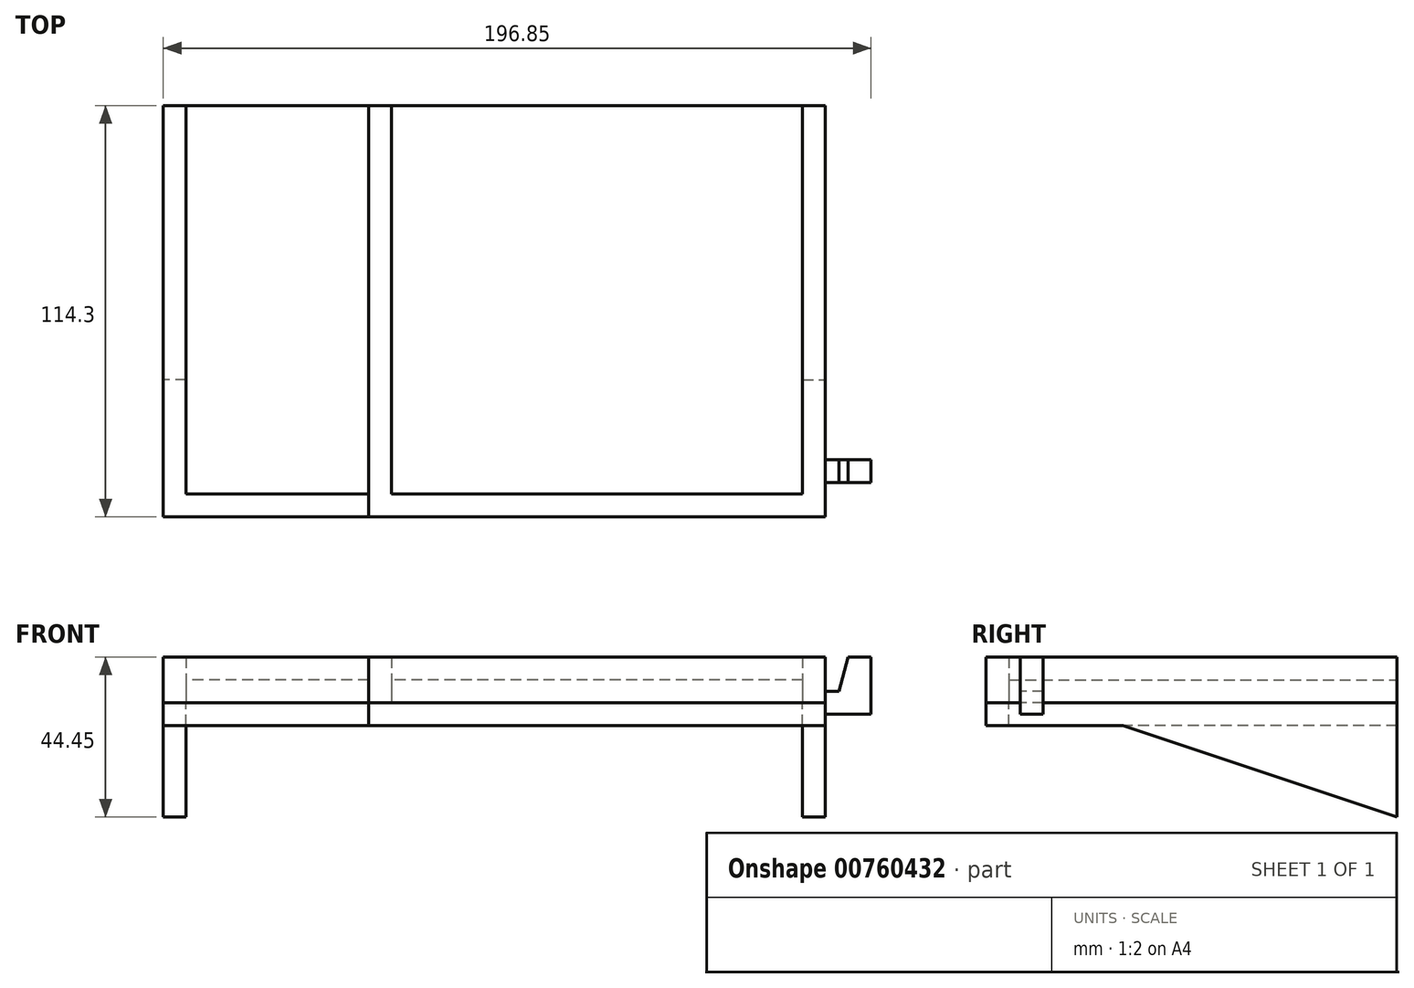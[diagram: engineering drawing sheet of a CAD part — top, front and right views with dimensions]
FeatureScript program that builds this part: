
annotation { "Feature Type Name" : "Feature", "Feature Type Description" : "" }
export const myFeature = defineFeature(function(context is Context, id is Id, definition is map)
    precondition{}
    {
        {
            var Q0;
            Q0=qCreatedBy(makeId("Top.planeOp"),FACE);
            var sketch = newSketch(context, id + "F0", { "sketchPlane" : qUnion([Q0])});
            skLineSegment(sketch, "E0.bottom", {"start": v(63.5, 57.15) * mm, "end": v(-63.5, 57.15) * mm});
            skLineSegment(sketch, "E0.top", {"start": v(63.5, -57.15) * mm, "end": v(-63.5, -57.15) * mm});
            skLineSegment(sketch, "E0.left", {"start": v(63.5, 57.15) * mm, "end": v(63.5, -57.15) * mm});
            skLineSegment(sketch, "E0.right", {"start": v(-63.5, 57.15) * mm, "end": v(-63.5, -57.15) * mm});
            skPoint(sketch, "E0.middle", {"position": v(0, 0) * mm});
            skLineSegment(sketch, "E1.bottom", {"start": v(-63.5, 57.15) * mm, "end": v(-57.15, 57.15) * mm});
            skLineSegment(sketch, "E1.top", {"start": v(-63.5, -57.15) * mm, "end": v(-57.15, -57.15) * mm});
            skLineSegment(sketch, "E1.right", {"start": v(-57.15, 57.15) * mm, "end": v(-57.15, -57.15) * mm});
            skLineSegment(sketch, "E2.bottom", {"start": v(-63.5, 57.15) * mm, "end": v(63.5, 57.15) * mm});
            skLineSegment(sketch, "E2.top", {"start": v(-63.5, 50.8) * mm, "end": v(63.5, 50.8) * mm});
            skLineSegment(sketch, "E2.left", {"start": v(-63.5, 57.15) * mm, "end": v(-63.5, 50.8) * mm});
            skLineSegment(sketch, "E2.right", {"start": v(63.5, 57.15) * mm, "end": v(63.5, 50.8) * mm});
            skLineSegment(sketch, "E3.bottom", {"start": v(-63.5, -57.15) * mm, "end": v(63.5, -57.15) * mm});
            skLineSegment(sketch, "E3.top", {"start": v(-63.5, -50.8) * mm, "end": v(63.5, -50.8) * mm});
            skLineSegment(sketch, "E3.left", {"start": v(-63.5, -57.15) * mm, "end": v(-63.5, -50.8) * mm});
            skLineSegment(sketch, "E3.right", {"start": v(63.5, -57.15) * mm, "end": v(63.5, -50.8) * mm});
            skLineSegment(sketch, "E4.bottom", {"start": v(63.5, -57.15) * mm, "end": v(57.15, -57.15) * mm});
            skLineSegment(sketch, "E4.top", {"start": v(63.5, 57.15) * mm, "end": v(57.15, 57.15) * mm});
            skLineSegment(sketch, "E4.left", {"start": v(63.5, -57.15) * mm, "end": v(63.5, 57.15) * mm});
            skLineSegment(sketch, "E4.right", {"start": v(57.15, -57.15) * mm, "end": v(57.15, 57.15) * mm});
            skLineSegment(sketch, "E5.bottom", {"start": v(-63.5, 57.15) * mm, "end": v(-114.3, 57.15) * mm});
            skLineSegment(sketch, "E5.left", {"start": v(-63.5, 57.15) * mm, "end": v(-63.5, -57.37) * mm});
            skLineSegment(sketch, "E5.right", {"start": v(-114.3, 57.15) * mm, "end": v(-114.3, -57.37) * mm});
            skLineSegment(sketch, "E6.bottom", {"start": v(-114.3, 57.15) * mm, "end": v(-120.65, 57.15) * mm});
            skLineSegment(sketch, "E6.top", {"start": v(-114.3, -57.15) * mm, "end": v(-120.65, -57.15) * mm});
            skLineSegment(sketch, "E6.left", {"start": v(-114.3, 57.15) * mm, "end": v(-114.3, -57.15) * mm});
            skLineSegment(sketch, "E6.right", {"start": v(-120.65, 57.15) * mm, "end": v(-120.65, -57.15) * mm});
            skLineSegment(sketch, "E7", {"start": v(-63.5, 50.8) * mm, "end": v(-114.3, 50.8) * mm});
            skLineSegment(sketch, "E8", {"start": v(-63.5, -50.8) * mm, "end": v(-63.5, 50.8) * mm});
            skLineSegment(sketch, "E9", {"start": v(-57.15, -57.15) * mm, "end": v(-57.15, 57.15) * mm});
            skLineSegment(sketch, "E10", {"start": v(-63.5, -50.8) * mm, "end": v(-114.3, -50.8) * mm});
            skLineSegment(sketch, "E11", {"start": v(-114.3, -50.8) * mm, "end": v(-114.3, -57.15) * mm});
            skLineSegment(sketch, "E12", {"start": v(-63.5, -57.15) * mm, "end": v(-114.3, -57.15) * mm});
            skSolve(sketch);
        }
        {
            var Q0;
            {var subQ0=sQuery(id+"F0.wireOp",EDGE,"E7");Q0=makeQuery(id+"F0.imprint","IMPRINT",FACE,{"disambiguationData":[TD([[makeQuery(id+"F0.imprint","IMPRINT",EDGE,{"derivedFrom":subQ0}),1.0]])]});}
            var Q1;
            {var subQ0=sQuery(id+"F0.wireOp",EDGE,"E2.top");var subQ1=sQuery(id+"F0.wireOp",EDGE,"E1.right");var subQ2=makeQuery(id+"F0.imprint","INTERSECT",VERTEX,{"derivedFrom":[subQ1,subQ0]});Q1=makeQuery(id+"F0.imprint","IMPRINT",FACE,{"disambiguationData":[TD([[makeQuery(id+"F0.imprint","IMPRINT",EDGE,{"disambiguationData":[TD([[subQ2,-1.0]])],"derivedFrom":subQ1}),1.0]])]});}
            var Q2;
            {var subQ0=sQuery(id+"F0.wireOp",EDGE,"E4.right");var subQ1=sQuery(id+"F0.wireOp",EDGE,"E0.bottom");var subQ2=makeQuery(id+"F0.imprint","INTERSECT",VERTEX,{"derivedFrom":[subQ1,subQ0]});Q2=makeQuery(id+"F0.imprint","IMPRINT",FACE,{"disambiguationData":[TD([[makeQuery(id+"F0.imprint","IMPRINT",EDGE,{"disambiguationData":[TD([[subQ2,-1.0]])],"derivedFrom":subQ1}),1.0]])]});}
            var Q3;
            {var subQ0=sQuery(id+"F0.wireOp",EDGE,"E5.bottom");Q3=makeQuery(id+"F0.imprint","IMPRINT",FACE,{"disambiguationData":[TD([[makeQuery(id+"F0.imprint","IMPRINT",EDGE,{"derivedFrom":subQ0}),1.0]])]});}
            extrude(context, id + "F1", {"entities" : qUnion([Q0, Q1, Q2, Q3]), "depth" : 6.35 * mm, "offsetDistance" : 25.4 * mm});
        }
        {
            var Q0;
            {var subQ3=sQuery(id+"F0.wireOp",EDGE,"E1.right");var subQ5=sQuery(id+"F0.wireOp",EDGE,"E2.top");var subQ7=makeQuery(id+"F0.imprint","INTERSECT",VERTEX,{"derivedFrom":[subQ3,subQ5]});Q0=makeQuery(id+"F0.imprint","IMPRINT",FACE,{"disambiguationData":[TD([[makeQuery(id+"F0.imprint","IMPRINT",EDGE,{"disambiguationData":[TD([[subQ7,1.0]])],"derivedFrom":subQ3}),-1.0]])]});}
            var Q1;
            {var subQ0=sQuery(id+"F0.wireOp",EDGE,"E2.top");var subQ5=sQuery(id+"F0.wireOp",EDGE,"E1.right");var subQ6=makeQuery(id+"F0.imprint","INTERSECT",VERTEX,{"derivedFrom":[subQ5,subQ0]});Q1=makeQuery(id+"F0.imprint","IMPRINT",FACE,{"disambiguationData":[TD([[makeQuery(id+"F0.imprint","IMPRINT",EDGE,{"disambiguationData":[TD([[subQ6,-1.0]])],"derivedFrom":subQ5}),-1.0]])]});}
            var Q2;
            {var subQ3=sQuery(id+"F0.wireOp",EDGE,"E5.top");Q2=makeQuery(id+"F0.imprint","IMPRINT",FACE,{"disambiguationData":[TD([[makeQuery(id+"F0.imprint","IMPRINT",EDGE,{"derivedFrom":subQ3}),-1.0]])]});}
            var Q3;
            {var subQ3=sQuery(id+"F0.wireOp",EDGE,"E1.right");var subQ5=sQuery(id+"F0.wireOp",EDGE,"E3.top");var subQ6=makeQuery(id+"F0.imprint","INTERSECT",VERTEX,{"derivedFrom":[subQ3,subQ5]});Q3=makeQuery(id+"F0.imprint","IMPRINT",FACE,{"disambiguationData":[TD([[makeQuery(id+"F0.imprint","IMPRINT",EDGE,{"disambiguationData":[TD([[subQ6,-1.0]])],"derivedFrom":subQ3}),-1.0]])]});}
            var Q4;
            {var subQ0=sQuery(id+"F0.wireOp",EDGE,"E4.right");var subQ1=sQuery(id+"F0.wireOp",EDGE,"E0.top");var subQ2=makeQuery(id+"F0.imprint","INTERSECT",VERTEX,{"derivedFrom":[subQ1,subQ0]});Q4=makeQuery(id+"F0.imprint","IMPRINT",FACE,{"disambiguationData":[TD([[makeQuery(id+"F0.imprint","IMPRINT",EDGE,{"disambiguationData":[TD([[subQ2,-1.0]])],"derivedFrom":subQ1}),-1.0]])]});}
            var Q5;
            {var subQ0=sQuery(id+"F0.wireOp",EDGE,"E2.top");var subQ1=sQuery(id+"F0.wireOp",EDGE,"E0.left");var subQ2=makeQuery(id+"F0.imprint","INTERSECT",VERTEX,{"derivedFrom":[subQ1,subQ0]});Q5=makeQuery(id+"F0.imprint","IMPRINT",FACE,{"disambiguationData":[TD([[makeQuery(id+"F0.imprint","IMPRINT",EDGE,{"disambiguationData":[TD([[subQ2,-1.0]])],"derivedFrom":subQ1}),-1.0]])]});}
            var Q6;
            {var subQ0=sQuery(id+"F0.wireOp",EDGE,"E4.right");var subQ1=sQuery(id+"F0.wireOp",EDGE,"E0.bottom");var subQ2=makeQuery(id+"F0.imprint","INTERSECT",VERTEX,{"derivedFrom":[subQ1,subQ0]});Q6=makeQuery(id+"F0.imprint","IMPRINT",FACE,{"disambiguationData":[TD([[makeQuery(id+"F0.imprint","IMPRINT",EDGE,{"disambiguationData":[TD([[subQ2,1.0]])],"derivedFrom":subQ1}),1.0]])]});}
            var Q7;
            {var subQ0=sQuery(id+"F0.wireOp",EDGE,"E4.right");var subQ1=sQuery(id+"F0.wireOp",EDGE,"E0.top");var subQ2=makeQuery(id+"F0.imprint","INTERSECT",VERTEX,{"derivedFrom":[subQ1,subQ0]});Q7=makeQuery(id+"F0.imprint","IMPRINT",FACE,{"disambiguationData":[TD([[makeQuery(id+"F0.imprint","IMPRINT",EDGE,{"disambiguationData":[TD([[subQ2,1.0]])],"derivedFrom":subQ1}),-1.0]])]});}
            extrude(context, id + "F2", {"entities" : qUnion([Q0, Q1, Q2, Q3, Q4, Q5, Q6, Q7]), "depth" : 12.7 * mm, "offsetDistance" : 25.4 * mm});
        }
        {
            var Q0;
            {var subQ0=sQuery(id+"F0.wireOp",EDGE,"E6.bottom");Q0=makeQuery(id+"F0.imprint","IMPRINT",FACE,{"disambiguationData":[TD([[makeQuery(id+"F0.imprint","IMPRINT",EDGE,{"derivedFrom":subQ0}),1.0]])]});}
            var Q1;
            {var subQ2=sQuery(id+"F0.wireOp",EDGE,"E10");Q1=makeQuery(id+"F0.imprint","IMPRINT",FACE,{"disambiguationData":[TD([[makeQuery(id+"F0.imprint","IMPRINT",EDGE,{"derivedFrom":subQ2}),1.0]])]});}
            extrude(context, id + "F3", {"entities" : qUnion([Q0, Q1]), "depth" : 12.7 * mm, "offsetDistance" : 25.4 * mm});
        }
        {
            var Q0;
            {var subQ3=sQuery(id+"F0.wireOp",EDGE,"E5.top");Q0=makeQuery(id+"F0.imprint","IMPRINT",FACE,{"disambiguationData":[TD([[makeQuery(id+"F0.imprint","IMPRINT",EDGE,{"derivedFrom":subQ3}),-1.0]])]});}
            var Q1;
            {var subQ3=sQuery(id+"F0.wireOp",EDGE,"E1.right");var subQ5=sQuery(id+"F0.wireOp",EDGE,"E3.top");var subQ6=makeQuery(id+"F0.imprint","INTERSECT",VERTEX,{"derivedFrom":[subQ3,subQ5]});Q1=makeQuery(id+"F0.imprint","IMPRINT",FACE,{"disambiguationData":[TD([[makeQuery(id+"F0.imprint","IMPRINT",EDGE,{"disambiguationData":[TD([[subQ6,-1.0]])],"derivedFrom":subQ3}),-1.0]])]});}
            var Q2;
            {var subQ0=sQuery(id+"F0.wireOp",EDGE,"E4.right");var subQ1=sQuery(id+"F0.wireOp",EDGE,"E0.top");var subQ2=makeQuery(id+"F0.imprint","INTERSECT",VERTEX,{"derivedFrom":[subQ1,subQ0]});Q2=makeQuery(id+"F0.imprint","IMPRINT",FACE,{"disambiguationData":[TD([[makeQuery(id+"F0.imprint","IMPRINT",EDGE,{"disambiguationData":[TD([[subQ2,-1.0]])],"derivedFrom":subQ1}),-1.0]])]});}
            var Q3;
            {var subQ0=sQuery(id+"F0.wireOp",EDGE,"E4.right");var subQ1=sQuery(id+"F0.wireOp",EDGE,"E0.top");var subQ2=makeQuery(id+"F0.imprint","INTERSECT",VERTEX,{"derivedFrom":[subQ1,subQ0]});Q3=makeQuery(id+"F0.imprint","IMPRINT",FACE,{"disambiguationData":[TD([[makeQuery(id+"F0.imprint","IMPRINT",EDGE,{"disambiguationData":[TD([[subQ2,1.0]])],"derivedFrom":subQ1}),-1.0]])]});}
            var Q4;
            {var subQ0=sQuery(id+"F0.wireOp",EDGE,"E2.top");var subQ1=sQuery(id+"F0.wireOp",EDGE,"E0.left");var subQ2=makeQuery(id+"F0.imprint","INTERSECT",VERTEX,{"derivedFrom":[subQ1,subQ0]});Q4=makeQuery(id+"F0.imprint","IMPRINT",FACE,{"disambiguationData":[TD([[makeQuery(id+"F0.imprint","IMPRINT",EDGE,{"disambiguationData":[TD([[subQ2,-1.0]])],"derivedFrom":subQ1}),-1.0]])]});}
            var Q5;
            {var subQ0=sQuery(id+"F0.wireOp",EDGE,"E4.right");var subQ1=sQuery(id+"F0.wireOp",EDGE,"E0.bottom");var subQ2=makeQuery(id+"F0.imprint","INTERSECT",VERTEX,{"derivedFrom":[subQ1,subQ0]});Q5=makeQuery(id+"F0.imprint","IMPRINT",FACE,{"disambiguationData":[TD([[makeQuery(id+"F0.imprint","IMPRINT",EDGE,{"disambiguationData":[TD([[subQ2,1.0]])],"derivedFrom":subQ1}),1.0]])]});}
            extrude(context, id + "F4", {"entities" : qUnion([Q0, Q1, Q2, Q3, Q4, Q5]), "oppositeDirection" : true, "depth" : 6.35 * mm, "offsetDistance" : 25.4 * mm});
        }
        {
            var Q0;
            {var subQ2=sQuery(id+"F0.wireOp",EDGE,"E10");Q0=makeQuery(id+"F0.imprint","IMPRINT",FACE,{"disambiguationData":[TD([[makeQuery(id+"F0.imprint","IMPRINT",EDGE,{"derivedFrom":subQ2}),1.0]])]});}
            var Q1;
            {var subQ0=sQuery(id+"F0.wireOp",EDGE,"E6.bottom");Q1=makeQuery(id+"F0.imprint","IMPRINT",FACE,{"disambiguationData":[TD([[makeQuery(id+"F0.imprint","IMPRINT",EDGE,{"derivedFrom":subQ0}),1.0]])]});}
            extrude(context, id + "F5", {"entities" : qUnion([Q0, Q1]), "oppositeDirection" : true, "depth" : 6.35 * mm, "offsetDistance" : 25.4 * mm});
        }
        {
            var Q0;
            Q0=makeQuery(id+"F4.opExtrude","SWEPT_FACE",FACE,{"disambiguationData":[OSD([sQuery(id+"F0.wireOp",EDGE,"E0.left")])]});
            var sketch = newSketch(context, id + "F6", { "sketchPlane" : qUnion([Q0])});
            skLineSegment(sketch, "E13", {"start": v(57.15, -6.35) * mm, "end": v(57.15, -31.75) * mm});
            skLineSegment(sketch, "E14", {"start": v(57.15, -6.35) * mm, "end": v(-19.05, -6.35) * mm});
            skLineSegment(sketch, "E15", {"start": v(-19.05, -6.35) * mm, "end": v(57.15, -31.75) * mm});
            skSolve(sketch);
        }
        {
            var Q0;
            Q0=makeQuery(id+"F6.imprint","IMPRINT",FACE,{"disambiguationData":[TD([[makeQuery(id+"F6.imprint","IMPRINT",EDGE,{"derivedFrom":sQuery(id+"F6.wireOp",EDGE,"E13")}),-1.0]])]});
            extrude(context, id + "F7", {"entities" : qUnion([Q0]), "operationType" : NewBodyOperationType.ADD, "oppositeDirection" : true, "depth" : 6.35 * mm, "offsetDistance" : 25.4 * mm});
        }
        {
            var Q0;
            Q0=makeQuery(id+"F5.opExtrude","SWEPT_FACE",FACE,{"disambiguationData":[OSD([sQuery(id+"F0.wireOp",EDGE,"E6.right")])]});
            var sketch = newSketch(context, id + "F8", { "sketchPlane" : qUnion([Q0])});
            skLineSegment(sketch, "E16", {"start": v(-57.15, -6.35) * mm, "end": v(-57.15, -31.75) * mm});
            skLineSegment(sketch, "E17", {"start": v(-57.15, -6.35) * mm, "end": v(19.05, -6.35) * mm});
            skLineSegment(sketch, "E18", {"start": v(19.05, -6.35) * mm, "end": v(-57.15, -31.75) * mm});
            skSolve(sketch);
        }
        {
            var Q0;
            Q0=makeQuery(id+"F8.imprint","IMPRINT",FACE,{"disambiguationData":[TD([[makeQuery(id+"F8.imprint","IMPRINT",EDGE,{"derivedFrom":sQuery(id+"F8.wireOp",EDGE,"E16")}),1.0]])]});
            extrude(context, id + "F9", {"entities" : qUnion([Q0]), "oppositeDirection" : true, "depth" : 6.35 * mm, "offsetDistance" : 25.4 * mm});
        }
        {
            var Q0;
            Q0=makeQuery(id+"F2.opExtrude","SWEPT_FACE",FACE,{"disambiguationData":[OSD([sQuery(id+"F0.wireOp",EDGE,"E0.left")])]});
            var sketch = newSketch(context, id + "F10", { "sketchPlane" : qUnion([Q0])});
            skLineSegment(sketch, "E19", {"start": v(-57.15, 0) * mm, "end": v(-44.45, 0) * mm});
            skLineSegment(sketch, "E20.bottom", {"start": v(-41.28, 3.17) * mm, "end": v(-47.63, 3.17) * mm});
            skLineSegment(sketch, "E20.top", {"start": v(-41.28, -3.18) * mm, "end": v(-47.63, -3.18) * mm});
            skLineSegment(sketch, "E20.left", {"start": v(-41.28, 3.17) * mm, "end": v(-41.28, -3.18) * mm});
            skLineSegment(sketch, "E20.right", {"start": v(-47.63, 3.17) * mm, "end": v(-47.63, -3.18) * mm});
            skPoint(sketch, "E20.middle", {"position": v(-44.45, 0) * mm});
            skSolve(sketch);
        }
        {
            var Q0;
            {var subQ1=sQuery(id+"F10.wireOp",EDGE,"E20.bottom");Q0=makeQuery(id+"F10.imprint","IMPRINT",FACE,{"disambiguationData":[TD([[makeQuery(id+"F10.imprint","IMPRINT",EDGE,{"derivedFrom":subQ1}),1.0]])]});}
            var Q1;
            {var subQ1=sQuery(id+"F10.wireOp",EDGE,"E20.top");Q1=makeQuery(id+"F10.imprint","IMPRINT",FACE,{"disambiguationData":[TD([[makeQuery(id+"F10.imprint","IMPRINT",EDGE,{"derivedFrom":subQ1}),-1.0]])]});}
            extrude(context, id + "F11", {"entities" : qUnion([Q0, Q1]), "depth" : 12.7 * mm, "offsetDistance" : 25.4 * mm});
        }
        {
            var Q0;
            Q0=makeQuery(id+"F11.opExtrude","SWEPT_FACE",FACE,{"disambiguationData":[OSD([sQuery(id+"F10.wireOp",EDGE,"E20.bottom")])]});
            var sketch = newSketch(context, id + "F12", { "sketchPlane" : qUnion([Q0])});
            skLineSegment(sketch, "E21.bottom", {"start": v(76.2, -47.62) * mm, "end": v(69.85, -47.62) * mm});
            skLineSegment(sketch, "E21.top", {"start": v(76.2, -41.27) * mm, "end": v(69.85, -41.27) * mm});
            skLineSegment(sketch, "E21.left", {"start": v(76.2, -47.62) * mm, "end": v(76.2, -41.27) * mm});
            skLineSegment(sketch, "E21.right", {"start": v(69.85, -47.62) * mm, "end": v(69.85, -41.27) * mm});
            skSolve(sketch);
        }
        {
            var Q0;
            Q0=makeQuery(id+"F12.imprint","IMPRINT",FACE,{"disambiguationData":[TD([[makeQuery(id+"F12.imprint","IMPRINT",EDGE,{"derivedFrom":sQuery(id+"F12.wireOp",EDGE,"E21.bottom")}),-1.0]])]});
            extrude(context, id + "F13", {"entities" : qUnion([Q0]), "operationType" : NewBodyOperationType.ADD, "depth" : 9.52 * mm, "offsetDistance" : 25.4 * mm});
        }
        {
            var Q0;
            Q0=makeQuery(id+"F13.boolean.opBoolean","MERGE",FACE,{"derivedFrom":[makeQuery(id+"F11.opExtrude","SWEPT_FACE",FACE,{"disambiguationData":[OSD([sQuery(id+"F10.wireOp",EDGE,"E20.right")])]}),makeQuery(id+"F13.opExtrude","SWEPT_FACE",FACE,{"disambiguationData":[OSD([sQuery(id+"F12.wireOp",EDGE,"E21.bottom")])]})]});
            var sketch = newSketch(context, id + "F14", { "sketchPlane" : qUnion([Q0])});
            skLineSegment(sketch, "E22", {"start": v(69.85, 3.17) * mm, "end": v(67.3, 3.17) * mm});
            skLineSegment(sketch, "E23", {"start": v(67.3, 3.17) * mm, "end": v(69.85, 12.7) * mm});
            skSolve(sketch);
        }
        {
            var Q0;
            Q0=makeQuery(id+"F14.imprint","IMPRINT",FACE,{"disambiguationData":[TD([[makeQuery(id+"F14.imprint","IMPRINT",EDGE,{"derivedFrom":sQuery(id+"F14.wireOp",EDGE,"E22")}),-1.0]])]});
            extrude(context, id + "F15", {"entities" : qUnion([Q0]), "operationType" : NewBodyOperationType.ADD, "oppositeDirection" : true, "depth" : 6.35 * mm, "offsetDistance" : 25.4 * mm});
        }
    });
